# Revit family: Faucet-Lavatory-Grohe-Eurosmart_Cosmopolitan_E-36328000
name_source: partatom
category: Plumbing Fixtures
revit_build: Autodesk Revit 2014 (Build: 20130308_1515(x64)
units: mm (PartAtom-declared; Revit-internal decimal feet)

## types (1)
- 36328000
    ADA Compliant = Yes
    Assembly Code = D2020300
    CW Connection = Yes
    CWFU = 1.5
    CalGreen Compliant = Yes
    Cold Water Connection Diameter = 3/8"
    Default Elevation = 0"
    Description = Eurosmart Cosmopolitan E
    Finish = Metal-Grohe-000-Chrome
    Flow Rate = 1.5 gpm (5.7 L/min)
    HW Connection = Yes
    HWFU = 1.5
    Height = 4 3/16"
    Hot Water Connection Diameter = 0"
    Installation Type = Deck-Mounted
    Length = 5 1/2"
    Manufacturer = Grohe
    Material = Metal-Grohe-000-Chrome
    Model = 36328000
    Price = Prices may vary. Please consult Manufacturer Representative for most up-to-date price list.
    Product Page URL = https://www.grohe.com
    Shipping Weight = 2.86 lb
    URL = http://www.grohe.com
    Vent Connection = No
    WFU = 0
    Warranty Documentation Link = https://cdn.cloud.grohe.com
    Waste Connection = No
    cUPC Compliant = Yes

## geometry (parser evidence)
native form markers: Sweep x1
no freeform markers — native parametric forms only
